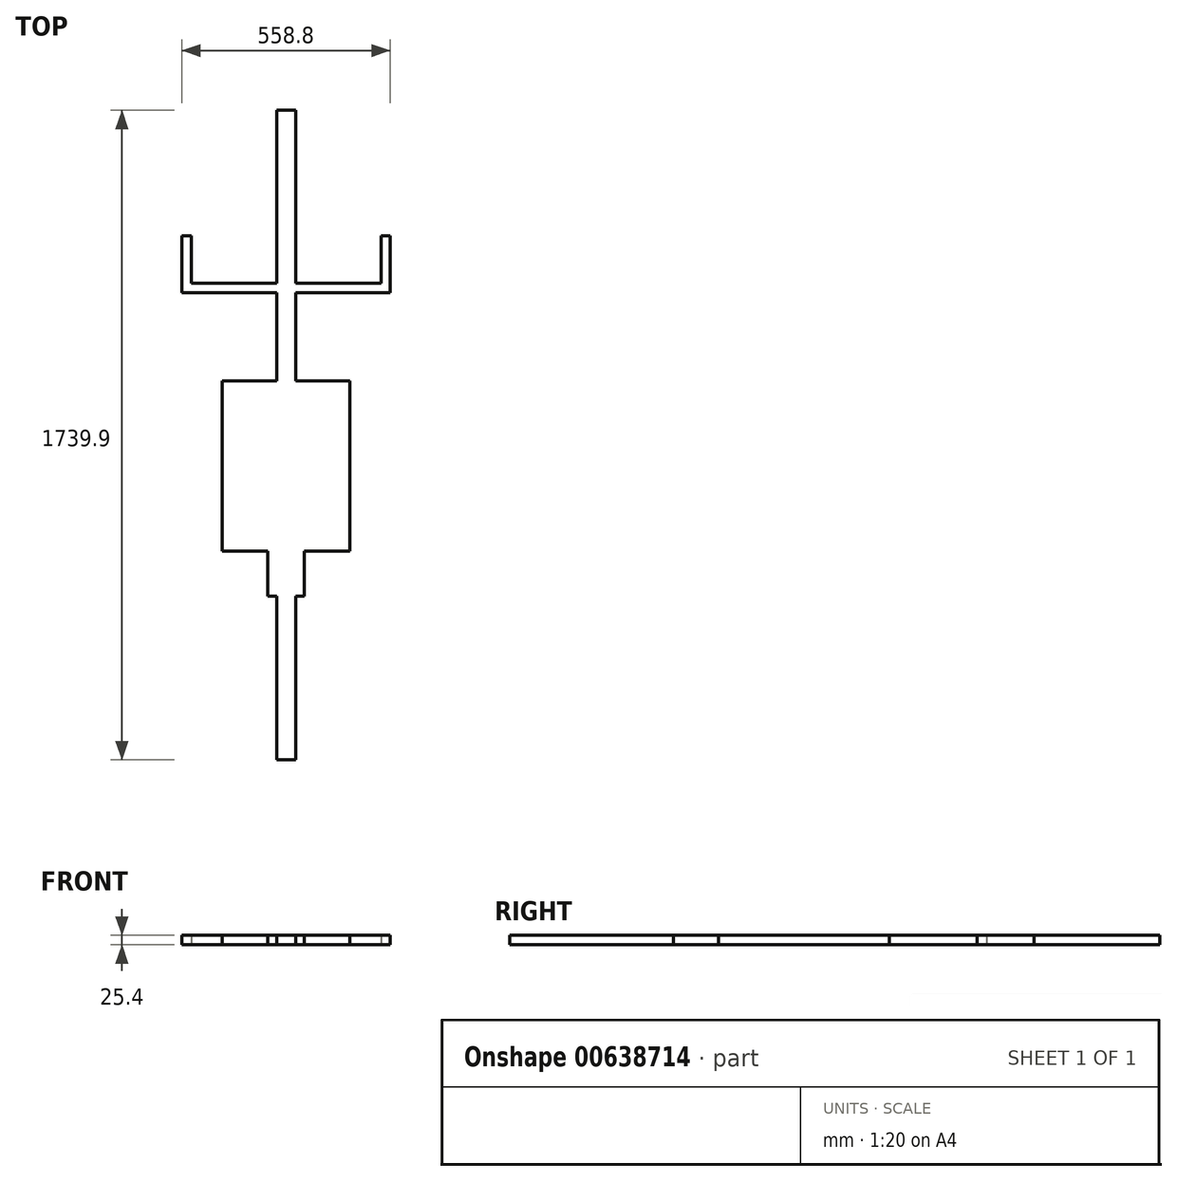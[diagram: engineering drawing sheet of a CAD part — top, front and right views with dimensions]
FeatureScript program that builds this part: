
annotation { "Feature Type Name" : "Feature", "Feature Type Description" : "" }
export const myFeature = defineFeature(function(context is Context, id is Id, definition is map)
    precondition{}
    {
        {
            var Q0;
            Q0=qCreatedBy(makeId("Top.planeOp"),FACE);
            var sketch = newSketch(context, id + "F0", { "sketchPlane" : qUnion([Q0])});
            skLineSegment(sketch, "E0.bottom", {"start": v(-25.4, 0) * mm, "end": v(25.4, 0) * mm});
            skLineSegment(sketch, "E0.top", {"start": v(-25.4, 1739.9) * mm, "end": v(25.4, 1739.9) * mm});
            skLineSegment(sketch, "E0.left", {"start": v(-25.4, 0) * mm, "end": v(-25.4, 1739.9) * mm});
            skLineSegment(sketch, "E0.right", {"start": v(25.4, 0) * mm, "end": v(25.4, 1739.9) * mm});
            skLineSegment(sketch, "E1.bottom", {"start": v(48.57, 438.15) * mm, "end": v(-48.57, 438.15) * mm});
            skLineSegment(sketch, "E1.top", {"start": v(48.57, 659.87) * mm, "end": v(-48.57, 659.87) * mm});
            skLineSegment(sketch, "E1.left", {"start": v(48.57, 438.15) * mm, "end": v(48.57, 659.87) * mm});
            skLineSegment(sketch, "E1.right", {"start": v(-48.57, 438.15) * mm, "end": v(-48.57, 659.87) * mm});
            skPoint(sketch, "E1.middle", {"position": v(0, 549.01) * mm});
            skLineSegment(sketch, "E2.bottom", {"start": v(279.4, 1250.95) * mm, "end": v(-279.4, 1250.95) * mm});
            skLineSegment(sketch, "E2.top", {"start": v(279.4, 1403.35) * mm, "end": v(254, 1403.35) * mm});
            skLineSegment(sketch, "E2.left", {"start": v(279.4, 1250.95) * mm, "end": v(279.4, 1403.35) * mm});
            skLineSegment(sketch, "E2.right", {"start": v(-279.4, 1250.95) * mm, "end": v(-279.4, 1403.35) * mm});
            skPoint(sketch, "E2.middle", {"position": v(0, 1327.15) * mm});
            skLineSegment(sketch, "E3.bottom", {"start": v(171.45, 558.8) * mm, "end": v(-171.45, 558.8) * mm});
            skLineSegment(sketch, "E3.top", {"start": v(171.45, 1015.55) * mm, "end": v(-171.45, 1015.55) * mm});
            skLineSegment(sketch, "E3.left", {"start": v(171.45, 558.8) * mm, "end": v(171.45, 1015.55) * mm});
            skLineSegment(sketch, "E3.right", {"start": v(-171.45, 558.8) * mm, "end": v(-171.45, 1015.55) * mm});
            skPoint(sketch, "E3.middle", {"position": v(0, 787.17) * mm});
            skLineSegment(sketch, "E4.bottom", {"start": v(254, 1276.35) * mm, "end": v(-254, 1276.35) * mm});
            skLineSegment(sketch, "E4.left", {"start": v(254, 1276.35) * mm, "end": v(254, 1403.35) * mm});
            skLineSegment(sketch, "E4.right", {"start": v(-254, 1276.35) * mm, "end": v(-254, 1403.35) * mm});
            skLineSegment(sketch, "E5.trimOffspring", {"start": v(-254, 1403.35) * mm, "end": v(-279.4, 1403.35) * mm});
            skSolve(sketch);
        }
        {
            var Q0;
            Q0=qSketchRegion(id+"F0",true);
            var Q1;
            {var subQ0=sQuery(id+"F0.wireOp",EDGE,"E3.bottom");var subQ1=sQuery(id+"F0.wireOp",EDGE,"E0.left");var subQ2=makeQuery(id+"F0.imprint","INTERSECT",VERTEX,{"derivedFrom":[subQ1,subQ0]});Q1=makeQuery(id+"F0.imprint","IMPRINT",FACE,{"disambiguationData":[TD([[makeQuery(id+"F0.imprint","IMPRINT",EDGE,{"disambiguationData":[TD([[subQ2,-1.0]])],"derivedFrom":subQ1}),-1.0]])]});}
            extrude(context, id + "F1", {"entities" : qUnion([Q0, Q1]), "depth" : 25.4 * mm, "offsetDistance" : 25.4 * mm});
        }
    });
